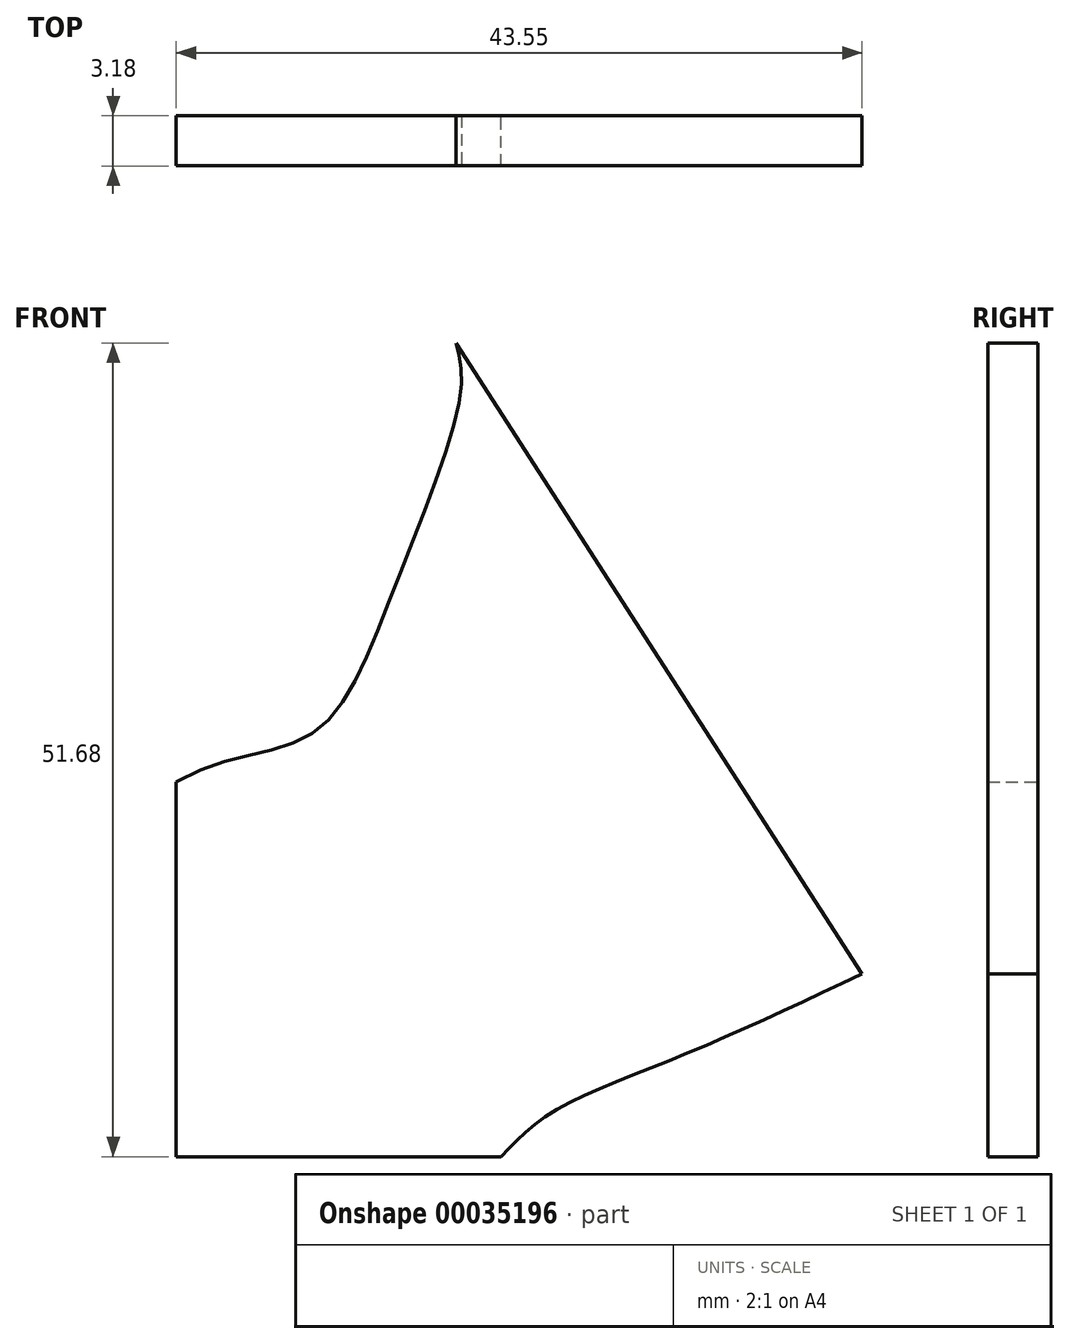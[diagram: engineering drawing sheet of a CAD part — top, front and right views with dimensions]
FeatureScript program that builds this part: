
annotation { "Feature Type Name" : "Feature", "Feature Type Description" : "" }
export const myFeature = defineFeature(function(context is Context, id is Id, definition is map)
    precondition{}
    {
        {
            var Q0;
            Q0=qCreatedBy(makeId("Front.planeOp"),FACE);
            var sketch = newSketch(context, id + "F0", { "sketchPlane" : qUnion([Q0])});
            skLineSegment(sketch, "E0", {"start": v(-20.64, 23.81) * mm, "end": v(-20.64, 0) * mm});
            skLineSegment(sketch, "E1", {"start": v(-20.64, 0) * mm, "end": v(0, 0) * mm});
            skFitSpline(sketch, "E2", {"points": [v(-20.64, 23.81) * mm, v(-12.1, 26.82) * mm, v(-7.02, 35.54) * mm, v(-2.6, 48.42) * mm, v(-2.86, 51.68) * mm], "startDerivative": vector(34.71, 21.08) * mm, "endDerivative": vector(-4.54, 17.47) * mm});
            skLineSegment(sketch, "E3", {"start": v(-2.86, 51.68) * mm, "end": v(22.9, 11.6) * mm});
            skFitSpline(sketch, "E4", {"points": [v(0, 0) * mm, v(3.13, 2.75) * mm, v(11.07, 6.26) * mm, v(22.9, 11.6) * mm], "startDerivative": vector(11.23, 11.99) * mm, "endDerivative": vector(28.86, 13.56) * mm});
            skSolve(sketch);
        }
        {
            var Q0;
            Q0=makeQuery(id+"F0.imprint","IMPRINT",FACE,{"disambiguationData":[TD([[makeQuery(id+"F0.imprint","IMPRINT",EDGE,{"derivedFrom":sQuery(id+"F0.wireOp",EDGE,"E0")}),1.0]])]});
            extrude(context, id + "F1", {"entities" : qUnion([Q0]), "depth" : 3.17 * mm});
        }
    });
